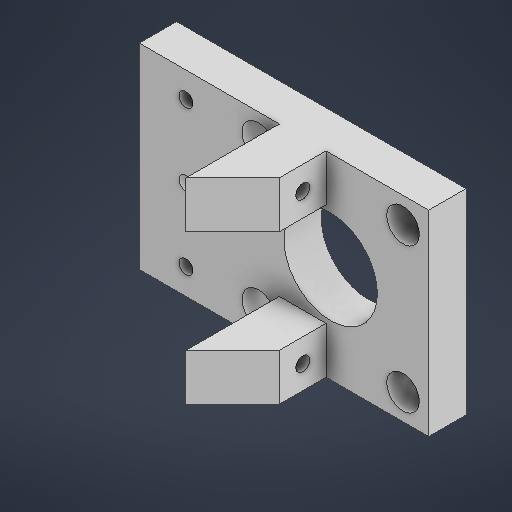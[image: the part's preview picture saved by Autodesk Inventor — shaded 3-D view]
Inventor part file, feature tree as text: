
AUTODESK INVENTOR PART (.ipt)
format: ipt  version: 2025.1 (Build 291241000, 241)  size: 279,552 bytes
history: native  units: mm
features: sketch x5, extrude x5, projected_geometry x4, draft x1
ambient origin geometry x8: Origin, YZ Plane, XZ Plane, XY Plane, X Axis, Y Axis, Z Axis, Center Point
bodies: Solid1 (feature_tree)
feature tree (15):
  sketch  "Sketch1"  dims[d0=42.0mm d1=42.0mm]
  extrude  "Extrusion1"  Depth=42.0mm
  extrude  "Extrusion3"  Depth=3.0mm
  extrude  "Extrusion4"  Depth=8.0mm TaperAngle=0.0deg
  extrude  "Extrusion5"  Depth=7.0mm
  extrude  "Extrusion6"  Depth=10.0mm
  draft  "FaceDraft1"
  sketch  "Sketch2"  dims[d2=31.0mm d3=3.0mm]
  projected_geometry  "Projected Loop1"
  sketch  "Sketch3"  dims[d4=3.0mm d5=8.0mm d6=0.0mm]
  projected_geometry  "Projected Loop2"
  sketch  "Sketch4"  dims[d7=20.0mm d10=7.0mm]
  sketch  "Sketch5"  dims[d11=5.0mm d12=0.0mm d13=10.0mm d14=10.0mm d15=10.0mm d16=10.0mm d17=0.0mm d18=31.0mm d19=10.0mm d20=10.0mm d21=3.0mm d22=10.0mm d23=0.0mm d24=3.0mm d25=3.0mm d26=0.0mm d27=0.0mm d28=45.0deg]
  projected_geometry  "Projected Loop3"
  projected_geometry  "Projected Loop4"
